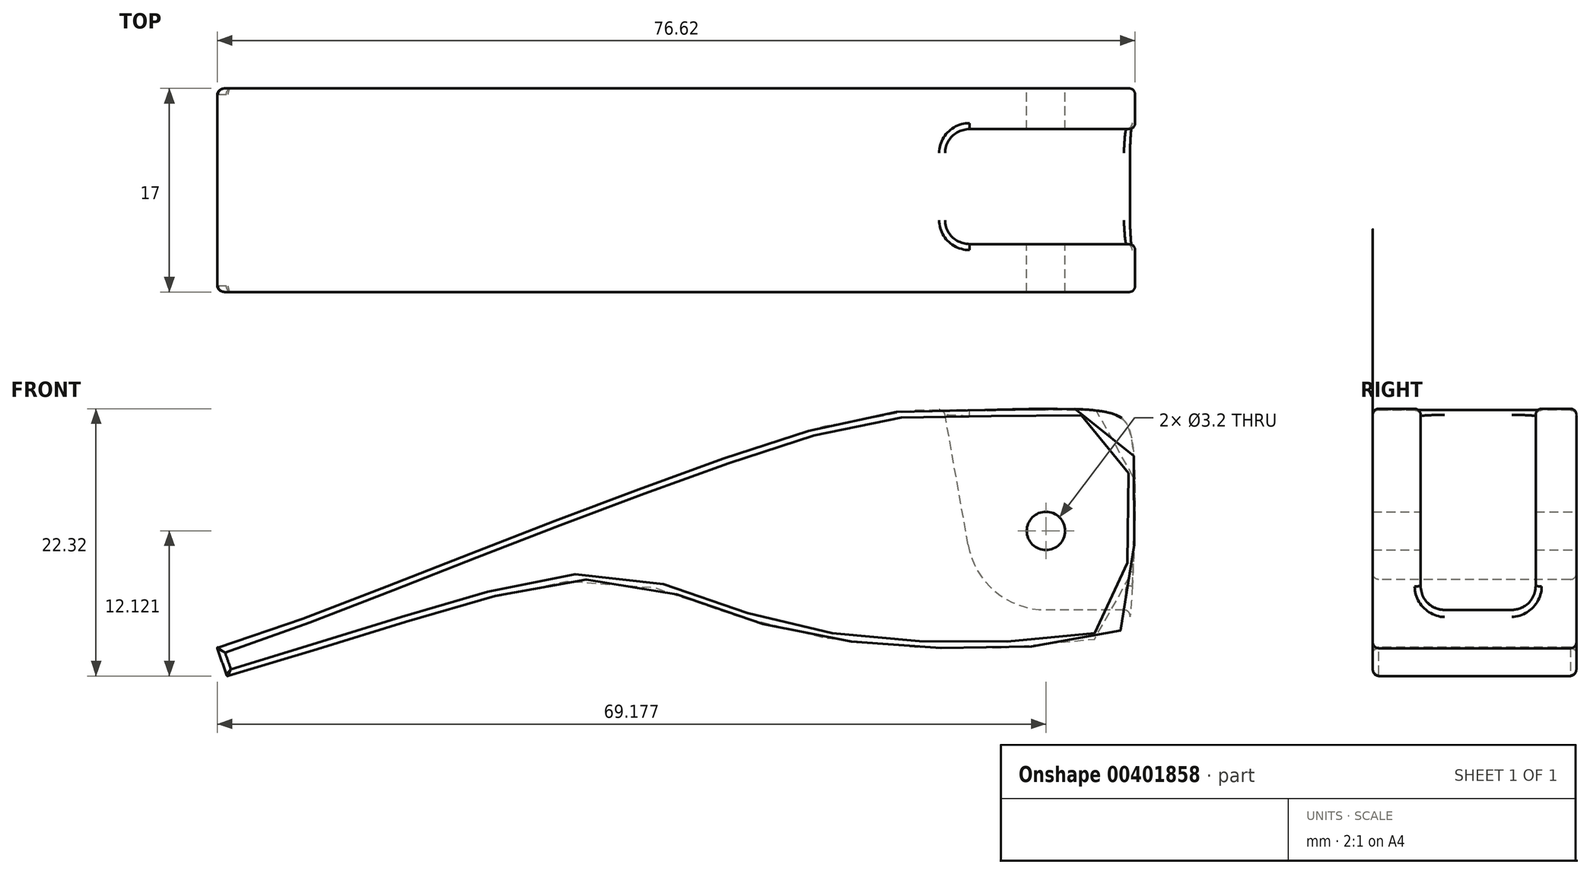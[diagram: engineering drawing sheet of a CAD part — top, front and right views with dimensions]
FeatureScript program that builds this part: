
annotation { "Feature Type Name" : "Feature", "Feature Type Description" : "" }
export const myFeature = defineFeature(function(context is Context, id is Id, definition is map)
    precondition{}
    {
        {
            var Q0;
            Q0=qCreatedBy(makeId("Front.planeOp"),FACE);
            var sketch = newSketch(context, id + "F0", { "sketchPlane" : qUnion([Q0])});
            skFitSpline(sketch, "E0", {"points": [v(9.52, 6.29) * mm, v(34.41, 6.4) * mm, v(35.81, 7.47) * mm, v(36.03, 8.76) * mm, v(36.14, 22.45) * mm, v(34.2, 24.93) * mm, v(22.78, 25.14) * mm, v(8.77, 23.3) * mm, v(-40.14, 5.32) * mm, v(-40.25, 5.32) * mm, v(-39.5, 3.05) * mm, v(-39.39, 2.95) * mm, v(-21.61, 8.33) * mm, v(-5.99, 10.81) * mm, v(9.52, 6.29) * mm]});
            skLineSegment(sketch, "E1", {"start": v(22.57, 5.26) * mm, "end": v(46.9, 5.26) * mm, "construction": true});
            skLineSegment(sketch, "E2", {"start": v(43.57, 25.26) * mm, "end": v(-2.33, 25.26) * mm, "construction": true});
            skCircle(sketch, "E3", {"center": v(28.93, 15.06) * mm, "radius": 1.6 * mm});
            skLineSegment(sketch, "E4", {"start": v(24.37, 13.46) * mm, "end": v(32.83, 13.46) * mm, "construction": true});
            skLineSegment(sketch, "E5", {"start": v(32.18, 16.66) * mm, "end": v(24, 16.66) * mm, "construction": true});
            skSolve(sketch);
        }
        {
            var Q0;
            Q0 = qSketchRegion(id + "F0", true);
            extrude(context, id + "F1", {"entities" : qUnion([Q0]), "depth" : 17 * mm});
        }
        {
            var Q0;
            Q0=makeQuery(id+"F1.opExtrude","CAP_FACE",FACE,{"disambiguationData":[OSD([sQuery(id+"F0.wireOp",EDGE,"E0"),sQuery(id+"F0.wireOp",EDGE,"E3")])],"isStart":false});
            cPlane(context, id + "F2", {"entities" : qUnion([Q0]), "cplaneType" : CPlaneType.OFFSET, "offset" : 4 * mm, "oppositeDirection" : true, "width" : 150 * mm, "height" : 150 * mm});
        }
        {
            var Q0;
            Q0=qCreatedBy(makeId("Right.planeOp"),FACE);
            cPlane(context, id + "F3", {"entities" : qUnion([Q0]), "cplaneType" : CPlaneType.OFFSET, "offset" : 25 * mm, "width" : 150 * mm, "height" : 150 * mm});
        }
        {
            var Q0;
            Q0=makeQuery(id+"F1.opExtrude","CAP_FACE",FACE,{"disambiguationData":[OSD([sQuery(id+"F0.wireOp",EDGE,"E0"),sQuery(id+"F0.wireOp",EDGE,"E3")])],"isStart":true});
            var sketch = newSketch(context, id + "F4", { "sketchPlane" : qUnion([Q0])});
            skLineSegment(sketch, "E6", {"start": v(-39.46, 25.26) * mm, "end": v(-10.53, 25.26) * mm, "construction": true});
            skLineSegment(sketch, "E7", {"start": v(-38.4, 16.67) * mm, "end": v(-18.35, 16.65) * mm, "construction": true});
            skLineSegment(sketch, "E8", {"start": v(-18.38, 13.46) * mm, "end": v(-39.3, 13.46) * mm, "construction": true});
            skLineSegment(sketch, "E9", {"start": v(-40.06, 5.26) * mm, "end": v(-6.34, 5.26) * mm, "construction": true});
            skLineSegment(sketch, "E10", {"start": v(-27.33, 7.56) * mm, "end": v(-27.33, 21.98) * mm, "construction": true});
            skPoint(sketch, "E11", {"position": v(-28.93, 15.06) * mm});
            skSolve(sketch);
        }
        {
            var Q0;
            Q0=qCreatedBy(id+"F3.planeOp",FACE);
            var Q1;
            Q1=sQuery(id+"F4.wireOp",VERTEX,"E11");
            cPlane(context, id + "F5", {"entities" : qUnion([Q0, Q1]), "cplaneType" : CPlaneType.PLANE_POINT, "offset" : 25 * mm, "width" : 150 * mm, "height" : 150 * mm});
        }
        {
            var Q0;
            Q0=qCreatedBy(id+"F2.planeOp",FACE);
            var sketch = newSketch(context, id + "F6", { "sketchPlane" : qUnion([Q0])});
            skCircle(sketch, "E12", {"center": v(28.93, 15.06) * mm, "radius": 6.6 * mm});
            skLineSegment(sketch, "E13", {"start": v(28.93, 15.06) * mm, "end": v(24.98, 37.26) * mm, "construction": true});
            skLineSegment(sketch, "E14", {"start": v(22.43, 13.9) * mm, "end": v(19, 33.15) * mm});
            skLineSegment(sketch, "E15", {"start": v(19, 33.15) * mm, "end": v(38.29, 26.31) * mm});
            skLineSegment(sketch, "E16", {"start": v(38.29, 26.31) * mm, "end": v(38.29, 8.46) * mm});
            skLineSegment(sketch, "E17", {"start": v(38.29, 8.46) * mm, "end": v(28.93, 8.46) * mm});
            skSolve(sketch);
        }
        {
            var Q0;
            Q0 = qSketchRegion(id + "F6", true);
            extrude(context, id + "F7", {"entities" : qUnion([Q0]), "operationType" : NewBodyOperationType.REMOVE, "oppositeDirection" : true, "depth" : 9.6 * mm});
        }
        {
            var Q0;
            Q0=makeQuery(id+"F7.boolean.opBoolean","COPY",EDGE,{"derivedFrom":makeQuery(id+"F7.opExtrude","CAP_EDGE",EDGE,{"disambiguationData":[OSD([sQuery(id+"F6.wireOp",EDGE,"E12")])],"isStart":true})});
            var Q1;
            Q1=makeQuery(id+"F7.boolean.opBoolean","COPY",EDGE,{"derivedFrom":makeQuery(id+"F7.opExtrude","CAP_EDGE",EDGE,{"disambiguationData":[OSD([sQuery(id+"F6.wireOp",EDGE,"E12")])],"isStart":false})});
            fillet(context, id + "F8", {"entities" : qUnion([Q0, Q1]), "radius" : 2 * mm, "tangentPropagation" : true, "allowEdgeOverflow" : false});
        }
        {
            var Q0;
            Q0=makeQuery(id+"F1.opExtrude","CAP_EDGE",EDGE,{"disambiguationData":[OSD([sQuery(id+"F0.wireOp",EDGE,"E0")])],"isStart":true});
            var Q1;
            Q1=makeQuery(id+"F1.opExtrude","CAP_EDGE",EDGE,{"disambiguationData":[OSD([sQuery(id+"F0.wireOp",EDGE,"E0")])],"isStart":false});
            var Q2;
            Q2=makeQuery(id+"F1.opExtrude","SWEPT_FACE",FACE,{"disambiguationData":[OSD([sQuery(id+"F0.wireOp",EDGE,"E0")])]});
            fillet(context, id + "F9", {"entities" : qUnion([Q0, Q1, Q2]), "radius" : 0.5 * mm, "tangentPropagation" : true, "allowEdgeOverflow" : false});
        }
    });
